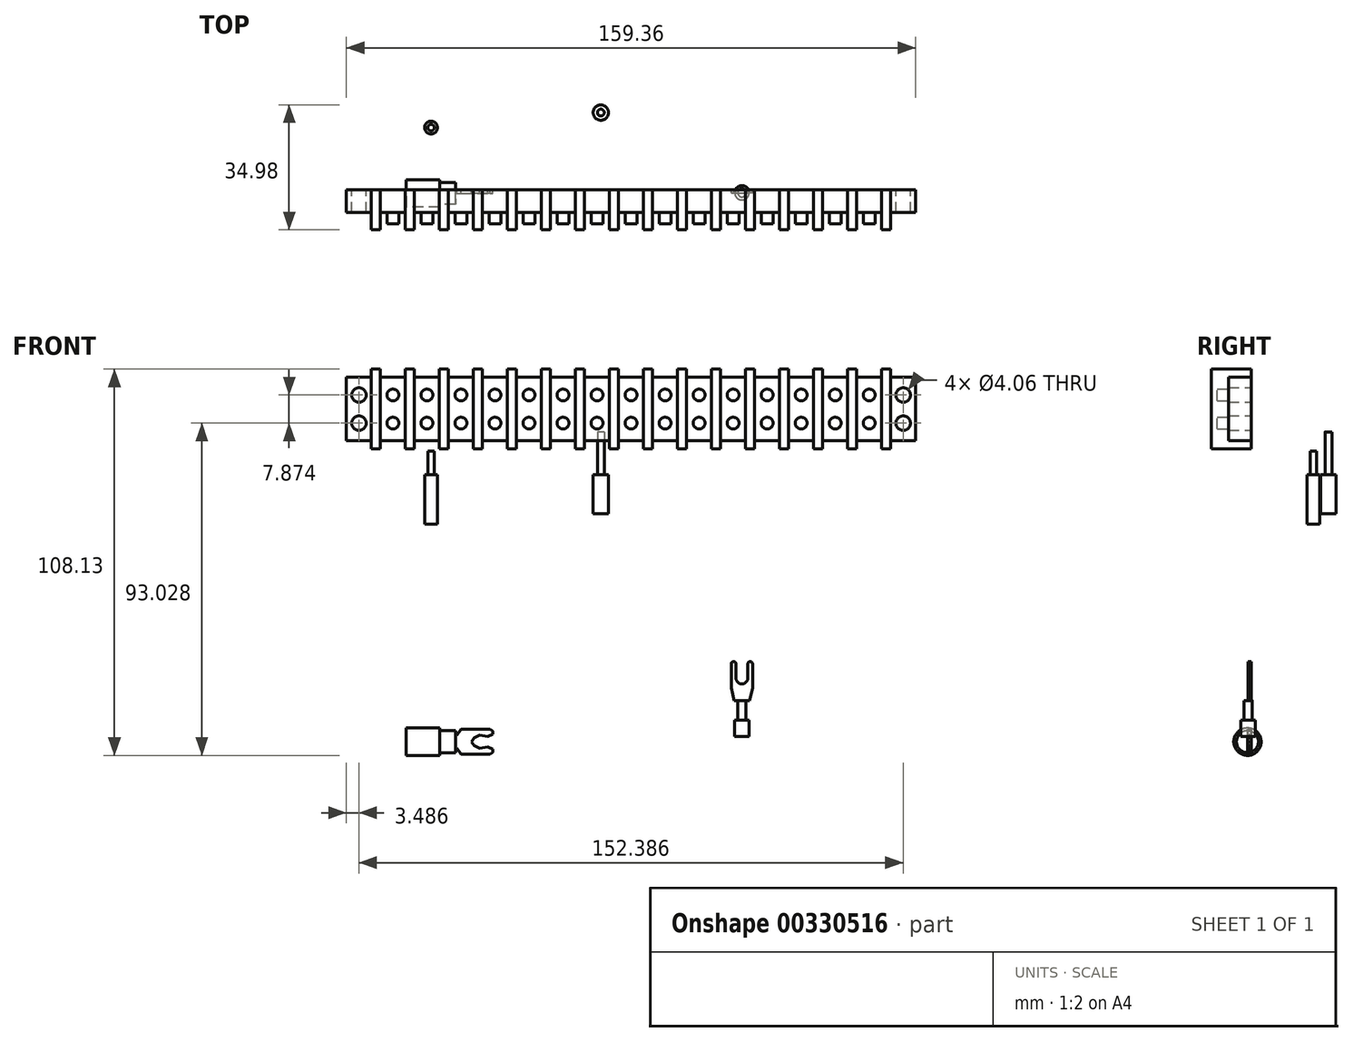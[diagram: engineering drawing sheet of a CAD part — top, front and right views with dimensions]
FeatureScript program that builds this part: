
annotation { "Feature Type Name" : "Feature", "Feature Type Description" : "" }
export const myFeature = defineFeature(function(context is Context, id is Id, definition is map)
    precondition{}
    {
        {
            var Q0;
            Q0=qCreatedBy(makeId("Front.planeOp"),FACE);
            var sketch = newSketch(context, id + "F0", { "sketchPlane" : qUnion([Q0])});
            skLineSegment(sketch, "E0.bottom", {"start": v(-35.8, 27.22) * mm, "end": v(-28.84, 27.22) * mm});
            skLineSegment(sketch, "E0.top", {"start": v(-35.8, 9.44) * mm, "end": v(-28.84, 9.44) * mm});
            skLineSegment(sketch, "E0.left", {"start": v(-35.8, 27.22) * mm, "end": v(-35.8, 9.44) * mm});
            skLineSegment(sketch, "E1", {"start": v(-35.8, 18.33) * mm, "end": v(-28.84, 18.33) * mm, "construction": true});
            skLineSegment(sketch, "E2", {"start": v(-32.32, 18.33) * mm, "end": v(-32.32, 22.27) * mm, "construction": true});
            skCircle(sketch, "E3", {"center": v(-32.32, 22.27) * mm, "radius": 2.03 * mm});
            skCircle(sketch, "E4.MirrorC", {"center": v(-32.32, 14.4) * mm, "radius": 2.03 * mm});
            skLineSegment(sketch, "E5", {"start": v(-28.84, 27.22) * mm, "end": v(-28.84, 9.44) * mm});
            skLineSegment(sketch, "E6.bottom", {"start": v(-28.84, 29.5) * mm, "end": v(-26.3, 29.5) * mm});
            skLineSegment(sketch, "E6.top", {"start": v(-28.84, 7.17) * mm, "end": v(-26.3, 7.17) * mm});
            skLineSegment(sketch, "E6.left", {"start": v(-28.84, 29.5) * mm, "end": v(-28.84, 7.17) * mm});
            skLineSegment(sketch, "E6.right", {"start": v(-26.3, 29.5) * mm, "end": v(-26.3, 7.17) * mm});
            skPoint(sketch, "E6.middle", {"position": v(-27.57, 18.33) * mm});
            skLineSegment(sketch, "E7.bottom", {"start": v(-26.3, 27.22) * mm, "end": v(-19.31, 27.22) * mm});
            skLineSegment(sketch, "E7.top", {"start": v(-26.3, 9.44) * mm, "end": v(-19.31, 9.44) * mm});
            skLineSegment(sketch, "E7.left", {"start": v(-26.3, 27.22) * mm, "end": v(-26.3, 9.44) * mm});
            skLineSegment(sketch, "E7.right", {"start": v(-19.31, 27.22) * mm, "end": v(-19.31, 9.44) * mm});
            skPoint(sketch, "E7.middle", {"position": v(-22.8, 18.33) * mm});
            skLineSegment(sketch, "E8.1.0.0", {"start": v(-19.31, 29.5) * mm, "end": v(-19.31, 7.17) * mm});
            skLineSegment(sketch, "E8.1.0.1", {"start": v(-19.31, 29.5) * mm, "end": v(-16.77, 29.5) * mm});
            skLineSegment(sketch, "E8.1.0.2", {"start": v(-19.31, 7.17) * mm, "end": v(-16.77, 7.17) * mm});
            skLineSegment(sketch, "E8.1.0.3", {"start": v(-16.77, 29.5) * mm, "end": v(-16.77, 7.17) * mm});
            skLineSegment(sketch, "E8.1.0.4", {"start": v(-16.77, 9.44) * mm, "end": v(-9.79, 9.44) * mm});
            skLineSegment(sketch, "E8.1.0.5", {"start": v(-16.77, 27.22) * mm, "end": v(-9.79, 27.22) * mm});
            skLineSegment(sketch, "E8.1.0.6", {"start": v(-9.79, 27.22) * mm, "end": v(-9.79, 9.44) * mm});
            skLineSegment(sketch, "E8.2.0.0", {"start": v(-9.79, 29.5) * mm, "end": v(-9.79, 7.17) * mm});
            skLineSegment(sketch, "E8.2.0.1", {"start": v(-9.79, 29.5) * mm, "end": v(-7.25, 29.5) * mm});
            skLineSegment(sketch, "E8.2.0.2", {"start": v(-9.79, 7.17) * mm, "end": v(-7.25, 7.17) * mm});
            skLineSegment(sketch, "E8.2.0.3", {"start": v(-7.25, 29.5) * mm, "end": v(-7.25, 7.17) * mm});
            skLineSegment(sketch, "E8.2.0.4", {"start": v(-7.25, 9.44) * mm, "end": v(-0.26, 9.44) * mm});
            skLineSegment(sketch, "E8.2.0.5", {"start": v(-7.25, 27.22) * mm, "end": v(-0.26, 27.22) * mm});
            skLineSegment(sketch, "E8.2.0.6", {"start": v(-0.26, 27.22) * mm, "end": v(-0.26, 9.44) * mm});
            skLineSegment(sketch, "E8.3.0.0", {"start": v(-0.26, 29.5) * mm, "end": v(-0.26, 7.17) * mm});
            skLineSegment(sketch, "E8.3.0.1", {"start": v(-0.26, 29.5) * mm, "end": v(2.28, 29.5) * mm});
            skLineSegment(sketch, "E8.3.0.2", {"start": v(-0.26, 7.17) * mm, "end": v(2.28, 7.17) * mm});
            skLineSegment(sketch, "E8.3.0.3", {"start": v(2.28, 29.5) * mm, "end": v(2.28, 7.17) * mm});
            skLineSegment(sketch, "E8.3.0.4", {"start": v(2.28, 9.44) * mm, "end": v(9.26, 9.44) * mm});
            skLineSegment(sketch, "E8.3.0.5", {"start": v(2.28, 27.22) * mm, "end": v(9.26, 27.22) * mm});
            skLineSegment(sketch, "E8.3.0.6", {"start": v(9.26, 27.22) * mm, "end": v(9.26, 9.44) * mm});
            skLineSegment(sketch, "E8.4.0.0", {"start": v(9.26, 29.5) * mm, "end": v(9.26, 7.17) * mm});
            skLineSegment(sketch, "E8.4.0.1", {"start": v(9.26, 29.5) * mm, "end": v(11.8, 29.5) * mm});
            skLineSegment(sketch, "E8.4.0.2", {"start": v(9.26, 7.17) * mm, "end": v(11.8, 7.17) * mm});
            skLineSegment(sketch, "E8.4.0.3", {"start": v(11.8, 29.5) * mm, "end": v(11.8, 7.17) * mm});
            skLineSegment(sketch, "E8.4.0.4", {"start": v(11.8, 9.44) * mm, "end": v(18.79, 9.44) * mm});
            skLineSegment(sketch, "E8.4.0.5", {"start": v(11.8, 27.22) * mm, "end": v(18.79, 27.22) * mm});
            skLineSegment(sketch, "E8.4.0.6", {"start": v(18.79, 27.22) * mm, "end": v(18.79, 9.44) * mm});
            skLineSegment(sketch, "E8.5.0.0", {"start": v(18.79, 29.5) * mm, "end": v(18.79, 7.17) * mm});
            skLineSegment(sketch, "E8.5.0.1", {"start": v(18.79, 29.5) * mm, "end": v(21.33, 29.5) * mm});
            skLineSegment(sketch, "E8.5.0.2", {"start": v(18.79, 7.17) * mm, "end": v(21.33, 7.17) * mm});
            skLineSegment(sketch, "E8.5.0.3", {"start": v(21.33, 29.5) * mm, "end": v(21.33, 7.17) * mm});
            skLineSegment(sketch, "E8.5.0.4", {"start": v(21.33, 9.44) * mm, "end": v(28.31, 9.44) * mm});
            skLineSegment(sketch, "E8.5.0.5", {"start": v(21.33, 27.22) * mm, "end": v(28.31, 27.22) * mm});
            skLineSegment(sketch, "E8.5.0.6", {"start": v(28.31, 27.22) * mm, "end": v(28.31, 9.44) * mm});
            skLineSegment(sketch, "E8.6.0.0", {"start": v(28.31, 29.5) * mm, "end": v(28.31, 7.17) * mm});
            skLineSegment(sketch, "E8.6.0.1", {"start": v(28.31, 29.5) * mm, "end": v(30.85, 29.5) * mm});
            skLineSegment(sketch, "E8.6.0.2", {"start": v(28.31, 7.17) * mm, "end": v(30.85, 7.17) * mm});
            skLineSegment(sketch, "E8.6.0.3", {"start": v(30.85, 29.5) * mm, "end": v(30.85, 7.17) * mm});
            skLineSegment(sketch, "E8.6.0.4", {"start": v(30.85, 9.44) * mm, "end": v(37.84, 9.44) * mm});
            skLineSegment(sketch, "E8.6.0.5", {"start": v(30.85, 27.22) * mm, "end": v(37.84, 27.22) * mm});
            skLineSegment(sketch, "E8.6.0.6", {"start": v(37.84, 27.22) * mm, "end": v(37.84, 9.44) * mm});
            skLineSegment(sketch, "E8.7.0.0", {"start": v(37.84, 29.5) * mm, "end": v(37.84, 7.17) * mm});
            skLineSegment(sketch, "E8.7.0.1", {"start": v(37.84, 29.5) * mm, "end": v(40.38, 29.5) * mm});
            skLineSegment(sketch, "E8.7.0.2", {"start": v(37.84, 7.17) * mm, "end": v(40.38, 7.17) * mm});
            skLineSegment(sketch, "E8.7.0.3", {"start": v(40.38, 29.5) * mm, "end": v(40.38, 7.17) * mm});
            skLineSegment(sketch, "E8.7.0.4", {"start": v(40.38, 9.44) * mm, "end": v(47.36, 9.44) * mm});
            skLineSegment(sketch, "E8.7.0.5", {"start": v(40.38, 27.22) * mm, "end": v(47.36, 27.22) * mm});
            skLineSegment(sketch, "E8.7.0.6", {"start": v(47.36, 27.22) * mm, "end": v(47.36, 9.44) * mm});
            skLineSegment(sketch, "E8.8.0.0", {"start": v(47.36, 29.5) * mm, "end": v(47.36, 7.17) * mm});
            skLineSegment(sketch, "E8.8.0.1", {"start": v(47.36, 29.5) * mm, "end": v(49.9, 29.5) * mm});
            skLineSegment(sketch, "E8.8.0.2", {"start": v(47.36, 7.17) * mm, "end": v(49.9, 7.17) * mm});
            skLineSegment(sketch, "E8.8.0.3", {"start": v(49.9, 29.5) * mm, "end": v(49.9, 7.17) * mm});
            skLineSegment(sketch, "E8.8.0.4", {"start": v(49.9, 9.44) * mm, "end": v(56.89, 9.44) * mm});
            skLineSegment(sketch, "E8.8.0.5", {"start": v(49.9, 27.22) * mm, "end": v(56.89, 27.22) * mm});
            skLineSegment(sketch, "E8.8.0.6", {"start": v(56.89, 27.22) * mm, "end": v(56.89, 9.44) * mm});
            skLineSegment(sketch, "E8.9.0.0", {"start": v(56.89, 29.5) * mm, "end": v(56.89, 7.17) * mm});
            skLineSegment(sketch, "E8.9.0.1", {"start": v(56.89, 29.5) * mm, "end": v(59.43, 29.5) * mm});
            skLineSegment(sketch, "E8.9.0.2", {"start": v(56.89, 7.17) * mm, "end": v(59.43, 7.17) * mm});
            skLineSegment(sketch, "E8.9.0.3", {"start": v(59.43, 29.5) * mm, "end": v(59.43, 7.17) * mm});
            skLineSegment(sketch, "E8.9.0.4", {"start": v(59.43, 9.44) * mm, "end": v(66.41, 9.44) * mm});
            skLineSegment(sketch, "E8.9.0.5", {"start": v(59.43, 27.22) * mm, "end": v(66.41, 27.22) * mm});
            skLineSegment(sketch, "E8.9.0.6", {"start": v(66.41, 27.22) * mm, "end": v(66.41, 9.44) * mm});
            skLineSegment(sketch, "E8.10.0.0", {"start": v(66.41, 29.5) * mm, "end": v(66.41, 7.17) * mm});
            skLineSegment(sketch, "E8.10.0.1", {"start": v(66.41, 29.5) * mm, "end": v(68.95, 29.5) * mm});
            skLineSegment(sketch, "E8.10.0.2", {"start": v(66.41, 7.17) * mm, "end": v(68.95, 7.17) * mm});
            skLineSegment(sketch, "E8.10.0.3", {"start": v(68.95, 29.5) * mm, "end": v(68.95, 7.17) * mm});
            skLineSegment(sketch, "E8.10.0.4", {"start": v(68.95, 9.44) * mm, "end": v(75.94, 9.44) * mm});
            skLineSegment(sketch, "E8.10.0.5", {"start": v(68.95, 27.22) * mm, "end": v(75.94, 27.22) * mm});
            skLineSegment(sketch, "E8.10.0.6", {"start": v(75.94, 27.22) * mm, "end": v(75.94, 9.44) * mm});
            skLineSegment(sketch, "E8.11.0.0", {"start": v(75.94, 29.5) * mm, "end": v(75.94, 7.17) * mm});
            skLineSegment(sketch, "E8.11.0.1", {"start": v(75.94, 29.5) * mm, "end": v(78.48, 29.5) * mm});
            skLineSegment(sketch, "E8.11.0.2", {"start": v(75.94, 7.17) * mm, "end": v(78.48, 7.17) * mm});
            skLineSegment(sketch, "E8.11.0.3", {"start": v(78.48, 29.5) * mm, "end": v(78.48, 7.17) * mm});
            skLineSegment(sketch, "E8.11.0.4", {"start": v(78.48, 9.44) * mm, "end": v(85.46, 9.44) * mm});
            skLineSegment(sketch, "E8.11.0.5", {"start": v(78.48, 27.22) * mm, "end": v(85.46, 27.22) * mm});
            skLineSegment(sketch, "E8.11.0.6", {"start": v(85.46, 27.22) * mm, "end": v(85.46, 9.44) * mm});
            skLineSegment(sketch, "E8.12.0.0", {"start": v(85.46, 29.5) * mm, "end": v(85.46, 7.17) * mm});
            skLineSegment(sketch, "E8.12.0.1", {"start": v(85.46, 29.5) * mm, "end": v(88, 29.5) * mm});
            skLineSegment(sketch, "E8.12.0.2", {"start": v(85.46, 7.17) * mm, "end": v(88, 7.17) * mm});
            skLineSegment(sketch, "E8.12.0.3", {"start": v(88, 29.5) * mm, "end": v(88, 7.17) * mm});
            skLineSegment(sketch, "E8.12.0.4", {"start": v(88, 9.44) * mm, "end": v(94.99, 9.44) * mm});
            skLineSegment(sketch, "E8.12.0.5", {"start": v(88, 27.22) * mm, "end": v(94.99, 27.22) * mm});
            skLineSegment(sketch, "E8.12.0.6", {"start": v(94.99, 27.22) * mm, "end": v(94.99, 9.44) * mm});
            skLineSegment(sketch, "E8.13.0.0", {"start": v(94.99, 29.5) * mm, "end": v(94.99, 7.17) * mm});
            skLineSegment(sketch, "E8.13.0.1", {"start": v(94.99, 29.5) * mm, "end": v(97.53, 29.5) * mm});
            skLineSegment(sketch, "E8.13.0.2", {"start": v(94.99, 7.17) * mm, "end": v(97.53, 7.17) * mm});
            skLineSegment(sketch, "E8.13.0.3", {"start": v(97.53, 29.5) * mm, "end": v(97.53, 7.17) * mm});
            skLineSegment(sketch, "E8.13.0.4", {"start": v(97.53, 9.44) * mm, "end": v(104.51, 9.44) * mm});
            skLineSegment(sketch, "E8.13.0.5", {"start": v(97.53, 27.22) * mm, "end": v(104.51, 27.22) * mm});
            skLineSegment(sketch, "E8.13.0.6", {"start": v(104.51, 27.22) * mm, "end": v(104.51, 9.44) * mm});
            skLineSegment(sketch, "E8.14.0.0", {"start": v(104.51, 29.5) * mm, "end": v(104.51, 7.17) * mm});
            skLineSegment(sketch, "E8.14.0.1", {"start": v(104.51, 29.5) * mm, "end": v(107.05, 29.5) * mm});
            skLineSegment(sketch, "E8.14.0.2", {"start": v(104.51, 7.17) * mm, "end": v(107.05, 7.17) * mm});
            skLineSegment(sketch, "E8.14.0.3", {"start": v(107.05, 29.5) * mm, "end": v(107.05, 7.17) * mm});
            skLineSegment(sketch, "E8.14.0.4", {"start": v(107.05, 9.44) * mm, "end": v(114.04, 9.44) * mm});
            skLineSegment(sketch, "E8.14.0.5", {"start": v(107.05, 27.22) * mm, "end": v(114.04, 27.22) * mm});
            skLineSegment(sketch, "E8.14.0.6", {"start": v(114.04, 27.22) * mm, "end": v(114.04, 9.44) * mm});
            skLineSegment(sketch, "E8.direction1", {"start": v(-28.84, 7.17) * mm, "end": v(-19.31, 7.17) * mm, "construction": true});
            skLineSegment(sketch, "E9.0.15.0", {"start": v(114.04, 29.5) * mm, "end": v(114.04, 7.17) * mm});
            skLineSegment(sketch, "E9.3.15.0", {"start": v(114.04, 29.5) * mm, "end": v(116.58, 29.5) * mm});
            skLineSegment(sketch, "E9.6.15.0", {"start": v(114.04, 7.17) * mm, "end": v(116.58, 7.17) * mm});
            skLineSegment(sketch, "E9.9.15.0", {"start": v(116.58, 29.5) * mm, "end": v(116.58, 7.17) * mm});
            skLineSegment(sketch, "E10", {"start": v(43.87, 27.22) * mm, "end": v(43.87, 9.44) * mm, "construction": true});
            skCircle(sketch, "E11.MirrorC", {"center": v(120.06, 22.27) * mm, "radius": 2.03 * mm});
            skCircle(sketch, "E12.MirrorC", {"center": v(120.06, 14.4) * mm, "radius": 2.03 * mm});
            skLineSegment(sketch, "E13.MirrorCS", {"start": v(123.55, 27.22) * mm, "end": v(123.55, 9.44) * mm});
            skLineSegment(sketch, "E14.MirrorCS", {"start": v(123.55, 9.44) * mm, "end": v(116.58, 9.44) * mm});
            skLineSegment(sketch, "E15.MirrorCS", {"start": v(123.55, 27.22) * mm, "end": v(116.58, 27.22) * mm});
            skSolve(sketch);
        }
        {
            var Q0;
            Q0=qCreatedBy(makeId("Front.planeOp"),FACE);
            var sketch = newSketch(context, id + "F1", { "sketchPlane" : qUnion([Q0])});
            skLineSegment(sketch, "E16", {"start": v(-11.61, -72.91) * mm, "end": v(-4.9, -72.91) * mm});
            skLineSegment(sketch, "E17", {"start": v(-4.9, -72.91) * mm, "end": v(-3.78, -71.34) * mm});
            skLineSegment(sketch, "E18", {"start": v(-3.78, -71.34) * mm, "end": v(4.37, -71.34) * mm});
            skLineSegment(sketch, "E19", {"start": v(4.37, -71.34) * mm, "end": v(5.16, -71.86) * mm});
            skLineSegment(sketch, "E20", {"start": v(5.16, -71.86) * mm, "end": v(5.16, -72.67) * mm});
            skLineSegment(sketch, "E21", {"start": v(5.16, -72.67) * mm, "end": v(3.76, -73.36) * mm});
            skLineSegment(sketch, "E22", {"start": v(3.76, -73.36) * mm, "end": v(1.41, -72.93) * mm});
            skLineSegment(sketch, "E23", {"start": v(1.41, -72.93) * mm, "end": v(0, -73.76) * mm});
            skLineSegment(sketch, "E24", {"start": v(0, -73.76) * mm, "end": v(-0.77, -74.8) * mm});
            skLineSegment(sketch, "E25", {"start": v(-0.77, -74.8) * mm, "end": v(-5.26, -74.8) * mm, "construction": true});
            skLineSegment(sketch, "E26.MirrorCS", {"start": v(-11.61, -76.67) * mm, "end": v(-4.9, -76.67) * mm});
            skLineSegment(sketch, "E27.MirrorCS", {"start": v(-4.9, -76.67) * mm, "end": v(-3.78, -78.24) * mm});
            skLineSegment(sketch, "E28.MirrorCS", {"start": v(-3.78, -78.24) * mm, "end": v(4.37, -78.24) * mm});
            skLineSegment(sketch, "E29.MirrorCS", {"start": v(4.37, -78.24) * mm, "end": v(5.16, -77.72) * mm});
            skLineSegment(sketch, "E30.MirrorCS", {"start": v(5.16, -77.72) * mm, "end": v(5.16, -76.9) * mm});
            skLineSegment(sketch, "E31.MirrorCS", {"start": v(5.16, -76.9) * mm, "end": v(3.76, -76.22) * mm});
            skLineSegment(sketch, "E32.MirrorCS", {"start": v(3.76, -76.22) * mm, "end": v(1.41, -76.65) * mm});
            skLineSegment(sketch, "E33.MirrorCS", {"start": v(1.41, -76.65) * mm, "end": v(0, -75.82) * mm});
            skLineSegment(sketch, "E34.MirrorCS", {"start": v(0, -75.82) * mm, "end": v(-0.77, -74.8) * mm});
            skLineSegment(sketch, "E35", {"start": v(-11.61, -72.91) * mm, "end": v(-11.61, -76.67) * mm});
            skSolve(sketch);
        }
        {
            var Q0;
            Q0 = qSketchRegion(id + "F1", true);
            extrude(context, id + "F2", {"entities" : qUnion([Q0]), "depth" : 1.02 * mm});
        }
        {
            var Q0;
            Q0=makeQuery(id+"F2.opExtrude","SWEPT_FACE",FACE,{"disambiguationData":[OSD([sQuery(id+"F1.wireOp",EDGE,"E35")])]});
            var sketch = newSketch(context, id + "F3", { "sketchPlane" : qUnion([Q0])});
            skCircle(sketch, "E36", {"center": v(1.02, -74.8) * mm, "radius": 3.07 * mm});
            skSolve(sketch);
        }
        {
            var Q0;
            Q0 = qSketchRegion(id + "F3", true);
            extrude(context, id + "F4", {"entities" : qUnion([Q0]), "operationType" : NewBodyOperationType.ADD, "oppositeDirection" : true, "depth" : 6.3 * mm});
        }
        {
            var Q0;
            Q0=makeQuery(id+"F4.boolean.opBoolean","MERGE",FACE,{"derivedFrom":[makeQuery(id+"F2.opExtrude","SWEPT_FACE",FACE,{"disambiguationData":[OSD([sQuery(id+"F1.wireOp",EDGE,"E35")])]}),makeQuery(id+"F4.opExtrude","CAP_FACE",FACE,{"disambiguationData":[OSD([sQuery(id+"F3.wireOp",EDGE,"E36")])],"isStart":true})]});
            var sketch = newSketch(context, id + "F5", { "sketchPlane" : qUnion([Q0])});
            skCircle(sketch, "E37", {"center": v(1.02, -74.8) * mm, "radius": 3.84 * mm});
            skSolve(sketch);
        }
        {
            var Q0;
            Q0 = qSketchRegion(id + "F5", true);
            extrude(context, id + "F6", {"entities" : qUnion([Q0]), "operationType" : NewBodyOperationType.ADD, "oppositeDirection" : true, "depth" : 1.9 * mm, "hasSecondDirection" : true, "secondDirectionOppositeDirection" : false, "secondDirectionDepth" : 7.47 * mm});
        }
        {
            var Q0;
            Q0 = qSketchRegion(id + "F0", true);
            extrude(context, id + "F7", {"entities" : qUnion([Q0]), "depth" : 6.35 * mm});
        }
        {
            var Q0;
            {var subQ3=sQuery(id+"F0.wireOp",EDGE,"E6.bottom");Q0=makeQuery(id+"F0.imprint","IMPRINT",FACE,{"disambiguationData":[TD([[makeQuery(id+"F0.imprint","IMPRINT",EDGE,{"derivedFrom":subQ3}),-1.0]])]});}
            var Q1;
            {var subQ0=sQuery(id+"F0.wireOp",EDGE,"E8.1.0.1");Q1=makeQuery(id+"F0.imprint","IMPRINT",FACE,{"disambiguationData":[TD([[makeQuery(id+"F0.imprint","IMPRINT",EDGE,{"derivedFrom":subQ0}),-1.0]])]});}
            var Q2;
            {var subQ0=sQuery(id+"F0.wireOp",EDGE,"E8.2.0.1");Q2=makeQuery(id+"F0.imprint","IMPRINT",FACE,{"disambiguationData":[TD([[makeQuery(id+"F0.imprint","IMPRINT",EDGE,{"derivedFrom":subQ0}),-1.0]])]});}
            var Q3;
            {var subQ0=sQuery(id+"F0.wireOp",EDGE,"E8.3.0.1");Q3=makeQuery(id+"F0.imprint","IMPRINT",FACE,{"disambiguationData":[TD([[makeQuery(id+"F0.imprint","IMPRINT",EDGE,{"derivedFrom":subQ0}),-1.0]])]});}
            var Q4;
            {var subQ0=sQuery(id+"F0.wireOp",EDGE,"E8.4.0.1");Q4=makeQuery(id+"F0.imprint","IMPRINT",FACE,{"disambiguationData":[TD([[makeQuery(id+"F0.imprint","IMPRINT",EDGE,{"derivedFrom":subQ0}),-1.0]])]});}
            var Q5;
            {var subQ0=sQuery(id+"F0.wireOp",EDGE,"E8.5.0.1");Q5=makeQuery(id+"F0.imprint","IMPRINT",FACE,{"disambiguationData":[TD([[makeQuery(id+"F0.imprint","IMPRINT",EDGE,{"derivedFrom":subQ0}),-1.0]])]});}
            var Q6;
            {var subQ0=sQuery(id+"F0.wireOp",EDGE,"E8.6.0.1");Q6=makeQuery(id+"F0.imprint","IMPRINT",FACE,{"disambiguationData":[TD([[makeQuery(id+"F0.imprint","IMPRINT",EDGE,{"derivedFrom":subQ0}),-1.0]])]});}
            var Q7;
            {var subQ0=sQuery(id+"F0.wireOp",EDGE,"E8.7.0.1");Q7=makeQuery(id+"F0.imprint","IMPRINT",FACE,{"disambiguationData":[TD([[makeQuery(id+"F0.imprint","IMPRINT",EDGE,{"derivedFrom":subQ0}),-1.0]])]});}
            var Q8;
            {var subQ0=sQuery(id+"F0.wireOp",EDGE,"E8.8.0.1");Q8=makeQuery(id+"F0.imprint","IMPRINT",FACE,{"disambiguationData":[TD([[makeQuery(id+"F0.imprint","IMPRINT",EDGE,{"derivedFrom":subQ0}),-1.0]])]});}
            var Q9;
            {var subQ0=sQuery(id+"F0.wireOp",EDGE,"E8.9.0.1");Q9=makeQuery(id+"F0.imprint","IMPRINT",FACE,{"disambiguationData":[TD([[makeQuery(id+"F0.imprint","IMPRINT",EDGE,{"derivedFrom":subQ0}),-1.0]])]});}
            var Q10;
            {var subQ0=sQuery(id+"F0.wireOp",EDGE,"E8.10.0.1");Q10=makeQuery(id+"F0.imprint","IMPRINT",FACE,{"disambiguationData":[TD([[makeQuery(id+"F0.imprint","IMPRINT",EDGE,{"derivedFrom":subQ0}),-1.0]])]});}
            var Q11;
            {var subQ0=sQuery(id+"F0.wireOp",EDGE,"E8.11.0.1");Q11=makeQuery(id+"F0.imprint","IMPRINT",FACE,{"disambiguationData":[TD([[makeQuery(id+"F0.imprint","IMPRINT",EDGE,{"derivedFrom":subQ0}),-1.0]])]});}
            var Q12;
            {var subQ0=sQuery(id+"F0.wireOp",EDGE,"E8.12.0.1");Q12=makeQuery(id+"F0.imprint","IMPRINT",FACE,{"disambiguationData":[TD([[makeQuery(id+"F0.imprint","IMPRINT",EDGE,{"derivedFrom":subQ0}),-1.0]])]});}
            var Q13;
            {var subQ0=sQuery(id+"F0.wireOp",EDGE,"E8.13.0.1");Q13=makeQuery(id+"F0.imprint","IMPRINT",FACE,{"disambiguationData":[TD([[makeQuery(id+"F0.imprint","IMPRINT",EDGE,{"derivedFrom":subQ0}),-1.0]])]});}
            var Q14;
            {var subQ0=sQuery(id+"F0.wireOp",EDGE,"E8.14.0.1");Q14=makeQuery(id+"F0.imprint","IMPRINT",FACE,{"disambiguationData":[TD([[makeQuery(id+"F0.imprint","IMPRINT",EDGE,{"derivedFrom":subQ0}),-1.0]])]});}
            var Q15;
            {var subQ0=sQuery(id+"F0.wireOp",EDGE,"E9.3.15.0");Q15=makeQuery(id+"F0.imprint","IMPRINT",FACE,{"disambiguationData":[TD([[makeQuery(id+"F0.imprint","IMPRINT",EDGE,{"derivedFrom":subQ0}),-1.0]])]});}
            extrude(context, id + "F8", {"entities" : qUnion([Q0, Q1, Q2, Q3, Q4, Q5, Q6, Q7, Q8, Q9, Q10, Q11, Q12, Q13, Q14, Q15]), "operationType" : NewBodyOperationType.ADD, "depth" : 11.18 * mm});
        }
        {
            var Q0;
            Q0=qCreatedBy(makeId("Front.planeOp"),FACE);
            var sketch = newSketch(context, id + "F9", { "sketchPlane" : qUnion([Q0])});
            skLineSegment(sketch, "E38", {"start": v(71.9, -53.03) * mm, "end": v(71.9, -59.76) * mm});
            skLineSegment(sketch, "E39", {"start": v(71.9, -59.76) * mm, "end": v(72.71, -63.24) * mm});
            skLineSegment(sketch, "E40", {"start": v(72.71, -63.24) * mm, "end": v(74.9, -63.24) * mm});
            skLineSegment(sketch, "E41", {"start": v(73.25, -53.03) * mm, "end": v(73.25, -56.97) * mm});
            skLineSegment(sketch, "E42", {"start": v(74.9, -63.24) * mm, "end": v(74.9, -57.23) * mm, "construction": true});
            skLineSegment(sketch, "E43.MirrorCS", {"start": v(76.55, -53.03) * mm, "end": v(76.55, -56.97) * mm});
            skLineSegment(sketch, "E44.MirrorCS", {"start": v(77.9, -53.03) * mm, "end": v(77.9, -59.76) * mm});
            skLineSegment(sketch, "E45.MirrorCS", {"start": v(77.9, -59.76) * mm, "end": v(77.09, -63.24) * mm});
            skLineSegment(sketch, "E46.MirrorCS", {"start": v(77.09, -63.24) * mm, "end": v(74.9, -63.24) * mm});
            skArc(sketch, "E47", {"start": v(73.25, -56.97) * mm, "mid": v(74.9, -58.62) * mm, "end": v(76.55, -56.97) * mm});
            skArc(sketch, "E48", {"start": v(73.25, -53.03) * mm, "mid": v(72.58, -52.36) * mm, "end": v(71.9, -53.03) * mm});
            skArc(sketch, "E49.MirrorCS", {"start": v(76.55, -53.03) * mm, "mid": v(77.22, -52.36) * mm, "end": v(77.9, -53.03) * mm});
            skSolve(sketch);
        }
        {
            var Q0;
            Q0=makeQuery(id+"F9.imprint","IMPRINT",FACE,{"disambiguationData":[TD([[makeQuery(id+"F9.imprint","IMPRINT",EDGE,{"derivedFrom":sQuery(id+"F9.wireOp",EDGE,"E38")}),1.0]])]});
            extrude(context, id + "F10", {"entities" : qUnion([Q0]), "depth" : 0.81 * mm});
        }
        {
            var Q0;
            Q0=makeQuery(id+"F10.opExtrude","SWEPT_FACE",FACE,{"disambiguationData":[OSD([sQuery(id+"F9.wireOp",EDGE,"E40"),sQuery(id+"F9.wireOp",EDGE,"E46.MirrorCS")])]});
            var sketch = newSketch(context, id + "F11", { "sketchPlane" : qUnion([Q0])});
            skCircle(sketch, "E50", {"center": v(74.9, 0.81) * mm, "radius": 1.16 * mm});
            skSolve(sketch);
        }
        {
            var Q0;
            Q0 = qSketchRegion(id + "F11", true);
            extrude(context, id + "F12", {"entities" : qUnion([Q0]), "operationType" : NewBodyOperationType.ADD, "depth" : 5.5 * mm});
        }
        {
            var Q0;
            Q0=makeQuery(id+"F12.opExtrude","CAP_FACE",FACE,{"disambiguationData":[OSD([sQuery(id+"F11.wireOp",EDGE,"E50")])],"isStart":false});
            var sketch = newSketch(context, id + "F13", { "sketchPlane" : qUnion([Q0])});
            skCircle(sketch, "E51", {"center": v(74.9, 0.81) * mm, "radius": 2 * mm});
            skSolve(sketch);
        }
        {
            var Q0;
            Q0 = qSketchRegion(id + "F13", true);
            extrude(context, id + "F14", {"entities" : qUnion([Q0]), "operationType" : NewBodyOperationType.ADD, "depth" : 4.52 * mm});
        }
        {
            var Q0;
            {var subQ0=sQuery(id+"F0.wireOp",EDGE,"E7.top");var subQ1=sQuery(id+"F0.wireOp",EDGE,"E7.bottom");var subQ2=sQuery(id+"F0.wireOp",EDGE,"E6.right");var subQ3=sQuery(id+"F0.wireOp",EDGE,"E6.top");var subQ5=sQuery(id+"F0.wireOp",EDGE,"E6.bottom");var subQ6=sQuery(id+"F0.wireOp",EDGE,"E8.1.0.0");var subQ7=sQuery(id+"F0.wireOp",EDGE,"E8.1.0.1");var subQ8=sQuery(id+"F0.wireOp",EDGE,"E8.1.0.2");Q0=makeQuery(id+"F8.boolean.opBoolean","SPLIT",FACE,{"disambiguationData":[TD([makeQuery(id+"F7.opExtrude","SWEPT_FACE",FACE,{"disambiguationData":[OSD([subQ1])]})])],"derivedFrom":makeQuery(id+"F7.opExtrude","CAP_FACE",FACE,{"disambiguationData":[OSD([sQuery(id+"F0.wireOp",EDGE,"E0.bottom"),sQuery(id+"F0.wireOp",EDGE,"E0.top"),sQuery(id+"F0.wireOp",EDGE,"E0.left"),sQuery(id+"F0.wireOp",EDGE,"E3"),sQuery(id+"F0.wireOp",EDGE,"E4.MirrorC"),subQ5,subQ3,sQuery(id+"F0.wireOp",EDGE,"E6.left"),subQ2,subQ1,subQ0,subQ6,subQ7,subQ8,sQuery(id+"F0.wireOp",EDGE,"E8.1.0.3"),sQuery(id+"F0.wireOp",EDGE,"E8.1.0.4"),sQuery(id+"F0.wireOp",EDGE,"E8.1.0.5"),sQuery(id+"F0.wireOp",EDGE,"E8.2.0.0"),sQuery(id+"F0.wireOp",EDGE,"E8.2.0.1"),sQuery(id+"F0.wireOp",EDGE,"E8.2.0.2"),sQuery(id+"F0.wireOp",EDGE,"E8.2.0.3"),sQuery(id+"F0.wireOp",EDGE,"E8.2.0.4"),sQuery(id+"F0.wireOp",EDGE,"E8.2.0.5"),sQuery(id+"F0.wireOp",EDGE,"E8.3.0.0"),sQuery(id+"F0.wireOp",EDGE,"E8.3.0.1"),sQuery(id+"F0.wireOp",EDGE,"E8.3.0.2"),sQuery(id+"F0.wireOp",EDGE,"E8.3.0.3"),sQuery(id+"F0.wireOp",EDGE,"E8.3.0.4"),sQuery(id+"F0.wireOp",EDGE,"E8.3.0.5"),sQuery(id+"F0.wireOp",EDGE,"E8.4.0.0"),sQuery(id+"F0.wireOp",EDGE,"E8.4.0.1"),sQuery(id+"F0.wireOp",EDGE,"E8.4.0.2"),sQuery(id+"F0.wireOp",EDGE,"E8.4.0.3"),sQuery(id+"F0.wireOp",EDGE,"E8.4.0.4"),sQuery(id+"F0.wireOp",EDGE,"E8.4.0.5"),sQuery(id+"F0.wireOp",EDGE,"E8.5.0.0"),sQuery(id+"F0.wireOp",EDGE,"E8.5.0.1"),sQuery(id+"F0.wireOp",EDGE,"E8.5.0.2"),sQuery(id+"F0.wireOp",EDGE,"E8.5.0.3"),sQuery(id+"F0.wireOp",EDGE,"E8.5.0.4"),sQuery(id+"F0.wireOp",EDGE,"E8.5.0.5"),sQuery(id+"F0.wireOp",EDGE,"E8.6.0.0"),sQuery(id+"F0.wireOp",EDGE,"E8.6.0.1"),sQuery(id+"F0.wireOp",EDGE,"E8.6.0.2"),sQuery(id+"F0.wireOp",EDGE,"E8.6.0.3"),sQuery(id+"F0.wireOp",EDGE,"E8.6.0.4"),sQuery(id+"F0.wireOp",EDGE,"E8.6.0.5"),sQuery(id+"F0.wireOp",EDGE,"E8.7.0.0"),sQuery(id+"F0.wireOp",EDGE,"E8.7.0.1"),sQuery(id+"F0.wireOp",EDGE,"E8.7.0.2"),sQuery(id+"F0.wireOp",EDGE,"E8.7.0.3"),sQuery(id+"F0.wireOp",EDGE,"E8.7.0.4"),sQuery(id+"F0.wireOp",EDGE,"E8.7.0.5"),sQuery(id+"F0.wireOp",EDGE,"E8.8.0.0"),sQuery(id+"F0.wireOp",EDGE,"E8.8.0.1"),sQuery(id+"F0.wireOp",EDGE,"E8.8.0.2"),sQuery(id+"F0.wireOp",EDGE,"E8.8.0.3"),sQuery(id+"F0.wireOp",EDGE,"E8.8.0.4"),sQuery(id+"F0.wireOp",EDGE,"E8.8.0.5"),sQuery(id+"F0.wireOp",EDGE,"E8.9.0.0"),sQuery(id+"F0.wireOp",EDGE,"E8.9.0.1"),sQuery(id+"F0.wireOp",EDGE,"E8.9.0.2"),sQuery(id+"F0.wireOp",EDGE,"E8.9.0.3"),sQuery(id+"F0.wireOp",EDGE,"E8.9.0.4"),sQuery(id+"F0.wireOp",EDGE,"E8.9.0.5"),sQuery(id+"F0.wireOp",EDGE,"E8.10.0.0"),sQuery(id+"F0.wireOp",EDGE,"E8.10.0.1"),sQuery(id+"F0.wireOp",EDGE,"E8.10.0.2"),sQuery(id+"F0.wireOp",EDGE,"E8.10.0.3"),sQuery(id+"F0.wireOp",EDGE,"E8.10.0.4"),sQuery(id+"F0.wireOp",EDGE,"E8.10.0.5"),sQuery(id+"F0.wireOp",EDGE,"E8.11.0.0"),sQuery(id+"F0.wireOp",EDGE,"E8.11.0.1"),sQuery(id+"F0.wireOp",EDGE,"E8.11.0.2"),sQuery(id+"F0.wireOp",EDGE,"E8.11.0.3"),sQuery(id+"F0.wireOp",EDGE,"E8.11.0.4"),sQuery(id+"F0.wireOp",EDGE,"E8.11.0.5"),sQuery(id+"F0.wireOp",EDGE,"E8.12.0.0"),sQuery(id+"F0.wireOp",EDGE,"E8.12.0.1"),sQuery(id+"F0.wireOp",EDGE,"E8.12.0.2"),sQuery(id+"F0.wireOp",EDGE,"E8.12.0.3"),sQuery(id+"F0.wireOp",EDGE,"E8.12.0.4"),sQuery(id+"F0.wireOp",EDGE,"E8.12.0.5"),sQuery(id+"F0.wireOp",EDGE,"E8.13.0.0"),sQuery(id+"F0.wireOp",EDGE,"E8.13.0.1"),sQuery(id+"F0.wireOp",EDGE,"E8.13.0.2"),sQuery(id+"F0.wireOp",EDGE,"E8.13.0.3"),sQuery(id+"F0.wireOp",EDGE,"E8.13.0.4"),sQuery(id+"F0.wireOp",EDGE,"E8.13.0.5"),sQuery(id+"F0.wireOp",EDGE,"E8.14.0.0"),sQuery(id+"F0.wireOp",EDGE,"E8.14.0.1"),sQuery(id+"F0.wireOp",EDGE,"E8.14.0.2"),sQuery(id+"F0.wireOp",EDGE,"E8.14.0.3"),sQuery(id+"F0.wireOp",EDGE,"E8.14.0.4"),sQuery(id+"F0.wireOp",EDGE,"E8.14.0.5"),sQuery(id+"F0.wireOp",EDGE,"E9.0.15.0"),sQuery(id+"F0.wireOp",EDGE,"E9.3.15.0"),sQuery(id+"F0.wireOp",EDGE,"E9.6.15.0"),sQuery(id+"F0.wireOp",EDGE,"E9.9.15.0"),sQuery(id+"F0.wireOp",EDGE,"E11.MirrorC"),sQuery(id+"F0.wireOp",EDGE,"E12.MirrorC"),sQuery(id+"F0.wireOp",EDGE,"E13.MirrorCS"),sQuery(id+"F0.wireOp",EDGE,"E14.MirrorCS"),sQuery(id+"F0.wireOp",EDGE,"E15.MirrorCS")])],"isStart":false})});}
            var sketch = newSketch(context, id + "F15", { "sketchPlane" : qUnion([Q0])});
            skLineSegment(sketch, "E52.0.0", {"start": v(-26.3, 9.44) * mm, "end": v(-19.31, 9.44) * mm, "construction": true});
            skLineSegment(sketch, "E52.0.1", {"start": v(-19.31, 9.44) * mm, "end": v(-19.31, 27.22) * mm, "construction": true});
            skLineSegment(sketch, "E52.0.2", {"start": v(-19.31, 27.22) * mm, "end": v(-26.3, 27.22) * mm, "construction": true});
            skLineSegment(sketch, "E52.0.3", {"start": v(-26.3, 27.22) * mm, "end": v(-26.3, 9.44) * mm, "construction": true});
            skLineSegment(sketch, "E53", {"start": v(-22.8, 18.33) * mm, "end": v(-22.8, 22.27) * mm, "construction": true});
            skPoint(sketch, "E53.startSnap0", {"position": v(-22.8, 27.22) * mm});
            skPoint(sketch, "E53.startSnap1", {"position": v(-26.3, 18.33) * mm});
            skCircle(sketch, "E54", {"center": v(-22.8, 22.27) * mm, "radius": 1.65 * mm});
            skCircle(sketch, "E55.0.1.0", {"center": v(-22.8, 14.4) * mm, "radius": 1.65 * mm});
            skCircle(sketch, "E55.1.0.0", {"center": v(-13.28, 22.27) * mm, "radius": 1.65 * mm});
            skCircle(sketch, "E55.1.1.0", {"center": v(-13.28, 14.4) * mm, "radius": 1.65 * mm});
            skCircle(sketch, "E55.2.0.0", {"center": v(-3.76, 22.27) * mm, "radius": 1.65 * mm});
            skCircle(sketch, "E55.2.1.0", {"center": v(-3.76, 14.4) * mm, "radius": 1.65 * mm});
            skCircle(sketch, "E55.3.0.0", {"center": v(5.77, 22.27) * mm, "radius": 1.65 * mm});
            skCircle(sketch, "E55.3.1.0", {"center": v(5.77, 14.4) * mm, "radius": 1.65 * mm});
            skCircle(sketch, "E55.4.0.0", {"center": v(15.3, 22.27) * mm, "radius": 1.65 * mm});
            skCircle(sketch, "E55.4.1.0", {"center": v(15.3, 14.4) * mm, "radius": 1.65 * mm});
            skCircle(sketch, "E55.5.0.0", {"center": v(24.82, 22.27) * mm, "radius": 1.65 * mm});
            skCircle(sketch, "E55.5.1.0", {"center": v(24.82, 14.4) * mm, "radius": 1.65 * mm});
            skCircle(sketch, "E55.6.0.0", {"center": v(34.34, 22.27) * mm, "radius": 1.65 * mm});
            skCircle(sketch, "E55.6.1.0", {"center": v(34.34, 14.4) * mm, "radius": 1.65 * mm});
            skCircle(sketch, "E55.7.0.0", {"center": v(43.87, 22.27) * mm, "radius": 1.65 * mm});
            skCircle(sketch, "E55.7.1.0", {"center": v(43.87, 14.4) * mm, "radius": 1.65 * mm});
            skCircle(sketch, "E55.8.0.0", {"center": v(53.4, 22.27) * mm, "radius": 1.65 * mm});
            skCircle(sketch, "E55.8.1.0", {"center": v(53.4, 14.4) * mm, "radius": 1.65 * mm});
            skCircle(sketch, "E55.9.0.0", {"center": v(62.92, 22.27) * mm, "radius": 1.65 * mm});
            skCircle(sketch, "E55.9.1.0", {"center": v(62.92, 14.4) * mm, "radius": 1.65 * mm});
            skCircle(sketch, "E55.10.0.0", {"center": v(72.44, 22.27) * mm, "radius": 1.65 * mm});
            skCircle(sketch, "E55.10.1.0", {"center": v(72.44, 14.4) * mm, "radius": 1.65 * mm});
            skCircle(sketch, "E55.11.0.0", {"center": v(81.97, 22.27) * mm, "radius": 1.65 * mm});
            skCircle(sketch, "E55.11.1.0", {"center": v(81.97, 14.4) * mm, "radius": 1.65 * mm});
            skCircle(sketch, "E55.12.0.0", {"center": v(91.5, 22.27) * mm, "radius": 1.65 * mm});
            skCircle(sketch, "E55.12.1.0", {"center": v(91.5, 14.4) * mm, "radius": 1.65 * mm});
            skCircle(sketch, "E55.13.0.0", {"center": v(101.02, 22.27) * mm, "radius": 1.65 * mm});
            skCircle(sketch, "E55.13.1.0", {"center": v(101.02, 14.4) * mm, "radius": 1.65 * mm});
            skCircle(sketch, "E55.14.0.0", {"center": v(110.54, 22.27) * mm, "radius": 1.65 * mm});
            skCircle(sketch, "E55.14.1.0", {"center": v(110.54, 14.4) * mm, "radius": 1.65 * mm});
            skLineSegment(sketch, "E55.direction1", {"start": v(-22.8, 22.27) * mm, "end": v(-13.28, 22.27) * mm, "construction": true});
            skLineSegment(sketch, "E55.direction2", {"start": v(-22.8, 22.27) * mm, "end": v(-22.8, 14.4) * mm, "construction": true});
            skSolve(sketch);
        }
        {
            var Q0;
            Q0 = qSketchRegion(id + "F15", true);
            extrude(context, id + "F16", {"entities" : qUnion([Q0]), "operationType" : NewBodyOperationType.ADD, "depth" : 3.17 * mm});
        }
        {
            var Q0;
            Q0=qCreatedBy(makeId("Top.planeOp"),FACE);
            var sketch = newSketch(context, id + "F17", { "sketchPlane" : qUnion([Q0])});
            skCircle(sketch, "E56", {"center": v(35.4, 21.64) * mm, "radius": 0.95 * mm});
            skSolve(sketch);
        }
        {
            var Q0;
            Q0=makeQuery(id+"F17.imprint","IMPRINT",FACE,{"disambiguationData":[TD([[makeQuery(id+"F17.imprint","IMPRINT",EDGE,{"derivedFrom":sQuery(id+"F17.wireOp",EDGE,"E56")}),1.0]])]});
            var Q1;
            Q1=sQuery(id+"F17.wireOp",EDGE,"E56");
            extrude(context, id + "F18", {"entities" : qUnion([Q0]), "surfaceEntities" : qUnion([Q1]), "depth" : 11.94 * mm});
        }
        {
            var Q0;
            Q0=makeQuery(id+"F18.opExtrude","CAP_FACE",FACE,{"disambiguationData":[OSD([sQuery(id+"F17.wireOp",EDGE,"E56")])],"isStart":true});
            var sketch = newSketch(context, id + "F19", { "sketchPlane" : qUnion([Q0])});
            skCircle(sketch, "E57", {"center": v(35.4, -21.64) * mm, "radius": 2.16 * mm});
            skSolve(sketch);
        }
        {
            var Q0;
            Q0 = qSketchRegion(id + "F19", true);
            extrude(context, id + "F20", {"entities" : qUnion([Q0]), "operationType" : NewBodyOperationType.ADD, "depth" : 10.92 * mm});
        }
        {
            var Q0;
            Q0=qCreatedBy(makeId("Top.planeOp"),FACE);
            var sketch = newSketch(context, id + "F21", { "sketchPlane" : qUnion([Q0])});
            skCircle(sketch, "E58", {"center": v(-12.12, 17.45) * mm, "radius": 0.89 * mm});
            skSolve(sketch);
        }
        {
            var Q0;
            Q0 = qSketchRegion(id + "F21", true);
            extrude(context, id + "F22", {"entities" : qUnion([Q0]), "depth" : 6.6 * mm});
        }
        {
            var Q0;
            Q0=makeQuery(id+"F22.opExtrude","CAP_FACE",FACE,{"disambiguationData":[OSD([sQuery(id+"F21.wireOp",EDGE,"E58")])],"isStart":true});
            var sketch = newSketch(context, id + "F23", { "sketchPlane" : qUnion([Q0])});
            skCircle(sketch, "E59", {"center": v(-12.12, -17.45) * mm, "radius": 1.8 * mm});
            skSolve(sketch);
        }
        {
            var Q0;
            Q0 = qSketchRegion(id + "F23", true);
            extrude(context, id + "F24", {"entities" : qUnion([Q0]), "operationType" : NewBodyOperationType.ADD, "depth" : 13.94 * mm});
        }
        {
            var Q0;
            Q0=makeQuery(id+"F10.opExtrude","CAP_FACE",FACE,{"disambiguationData":[OSD([sQuery(id+"F9.wireOp",EDGE,"E38"),sQuery(id+"F9.wireOp",EDGE,"E39"),sQuery(id+"F9.wireOp",EDGE,"E40"),sQuery(id+"F9.wireOp",EDGE,"E41"),sQuery(id+"F9.wireOp",EDGE,"E43.MirrorCS"),sQuery(id+"F9.wireOp",EDGE,"E44.MirrorCS"),sQuery(id+"F9.wireOp",EDGE,"E45.MirrorCS"),sQuery(id+"F9.wireOp",EDGE,"E46.MirrorCS"),sQuery(id+"F9.wireOp",EDGE,"E47"),sQuery(id+"F9.wireOp",EDGE,"E48"),sQuery(id+"F9.wireOp",EDGE,"E49.MirrorCS")])],"isStart":true});
            var sketch = newSketch(context, id + "F25", { "sketchPlane" : qUnion([Q0])});
            skArc(sketch, "E60.0", {"start": v(-73.25, -56.97) * mm, "mid": v(-74.9, -58.62) * mm, "end": v(-76.55, -56.97) * mm, "construction": true});
            skLineSegment(sketch, "E61.bottom", {"start": v(-74.9, -56.97) * mm, "end": v(-80.04, -56.97) * mm, "construction": true});
            skLineSegment(sketch, "E61.top", {"start": v(-74.9, -52.34) * mm, "end": v(-80.04, -52.34) * mm, "construction": true});
            skLineSegment(sketch, "E61.left", {"start": v(-74.9, -56.97) * mm, "end": v(-74.9, -52.34) * mm, "construction": true});
            skLineSegment(sketch, "E61.right", {"start": v(-80.04, -56.97) * mm, "end": v(-80.04, -52.34) * mm, "construction": true});
            skSolve(sketch);
        }
    });
